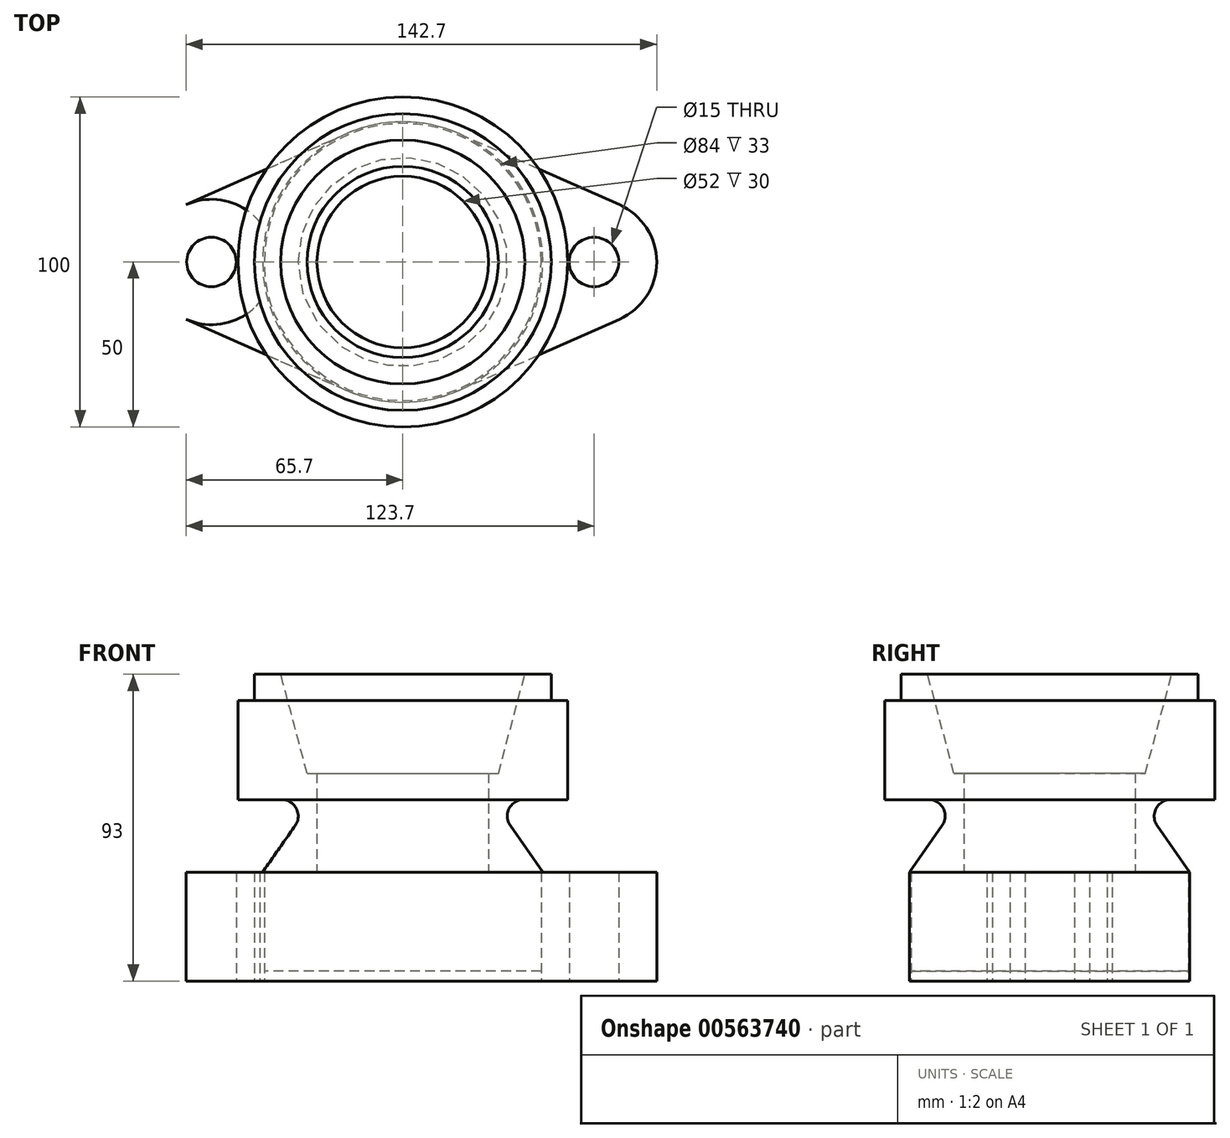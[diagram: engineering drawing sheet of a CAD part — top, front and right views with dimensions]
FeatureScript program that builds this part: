
annotation { "Feature Type Name" : "Feature", "Feature Type Description" : "" }
export const myFeature = defineFeature(function(context is Context, id is Id, definition is map)
    precondition{}
    {
        {
            var Q0;
            Q0=qCreatedBy(makeId("Top.planeOp"),FACE);
            var sketch = newSketch(context, id + "F0", { "sketchPlane" : qUnion([Q0])});
            skCircle(sketch, "E0", {"center": v(0, 0) * mm, "radius": 45 * mm});
            skCircle(sketch, "E1", {"center": v(0, 0) * mm, "radius": 42.5 * mm});
            skPoint(sketch, "E2", {"position": v(58, 0) * mm});
            skCircle(sketch, "E3", {"center": v(58, 0) * mm, "radius": 19 * mm});
            skCircle(sketch, "E4", {"center": v(58, 0) * mm, "radius": 7.5 * mm});
            skCircle(sketch, "E5.MirrorC", {"center": v(-58, 0) * mm, "radius": 7.5 * mm});
            skCircle(sketch, "E6.MirrorC", {"center": v(-58, 0) * mm, "radius": 19 * mm});
            skPoint(sketch, "E7", {"position": v(-20.17, 40.23) * mm});
            skPoint(sketch, "E8", {"position": v(20.17, 40.23) * mm});
            skPoint(sketch, "E9", {"position": v(20.17, -40.23) * mm});
            skPoint(sketch, "E10", {"position": v(-20.17, -40.23) * mm});
            skPoint(sketch, "E11", {"position": v(-77, 0) * mm});
            skPoint(sketch, "E12", {"position": v(73.15, 0) * mm});
            skLineSegment(sketch, "E13", {"start": v(-75.5, 13.02) * mm, "end": v(-3.42, 44.97) * mm});
            skLineSegment(sketch, "E14", {"start": v(12.58, 40.91) * mm, "end": v(100.28, 2.04) * mm});
            skLineSegment(sketch, "E15", {"start": v(-82.48, -9.93) * mm, "end": v(-3.7, -44.85) * mm});
            skLineSegment(sketch, "E16", {"start": v(12.55, -40.92) * mm, "end": v(81.15, -10.52) * mm});
            skCircle(sketch, "E17", {"center": v(0, 0) * mm, "radius": 42 * mm});
            skSolve(sketch);
        }
        {
            var Q0;
            Q0=qCreatedBy(makeId("Front.planeOp"),FACE);
            var sketch = newSketch(context, id + "F1", { "sketchPlane" : qUnion([Q0])});
            skLineSegment(sketch, "E18", {"start": v(-77, 0) * mm, "end": v(0, 0) * mm});
            skLineSegment(sketch, "E19", {"start": v(-77, 0) * mm, "end": v(-77, 33) * mm});
            skLineSegment(sketch, "E20", {"start": v(-77, 33) * mm, "end": v(-42.5, 33) * mm});
            skPoint(sketch, "E21", {"position": v(-42, 0) * mm});
            skLineSegment(sketch, "E22", {"start": v(-42, 0) * mm, "end": v(-42, 3) * mm});
            skLineSegment(sketch, "E23", {"start": v(-42, 3) * mm, "end": v(0, 3) * mm});
            skLineSegment(sketch, "E24", {"start": v(0, 2.9) * mm, "end": v(0, 3) * mm});
            skLineSegment(sketch, "E25", {"start": v(-42.5, 33) * mm, "end": v(-32.6, 47.13) * mm});
            skLineSegment(sketch, "E26", {"start": v(-36.7, 55) * mm, "end": v(-50, 55) * mm});
            skLineSegment(sketch, "E27", {"start": v(-50, 55) * mm, "end": v(-50, 85) * mm});
            skLineSegment(sketch, "E28", {"start": v(-50, 85) * mm, "end": v(-45, 85) * mm});
            skLineSegment(sketch, "E29", {"start": v(-45, 85) * mm, "end": v(-45, 93) * mm});
            skLineSegment(sketch, "E30", {"start": v(-45, 93) * mm, "end": v(-37, 93) * mm});
            skLineSegment(sketch, "E31", {"start": v(-29, 63) * mm, "end": v(-26, 63) * mm});
            skPoint(sketch, "E32", {"position": v(-29, 63) * mm});
            skLineSegment(sketch, "E33", {"start": v(-37, 93) * mm, "end": v(-29, 63) * mm});
            skPoint(sketch, "E34", {"position": v(-26, 63) * mm});
            skLineSegment(sketch, "E35", {"start": v(-26, 63) * mm, "end": v(-26, 21) * mm});
            skLineSegment(sketch, "E36", {"start": v(-26, 21) * mm, "end": v(0, 21) * mm});
            skLineSegment(sketch, "E37", {"start": v(0, 21) * mm, "end": v(0, 3) * mm});
            skLineSegment(sketch, "E38", {"start": v(-36.7, 59.99) * mm, "end": v(-36.7, 50) * mm, "construction": true});
            skLineSegment(sketch, "E39", {"start": v(-36.7, 50) * mm, "end": v(-27.85, 43.8) * mm, "construction": true});
            skPoint(sketch, "E40", {"position": v(-36.7, 55) * mm});
            skPoint(sketch, "E41", {"position": v(-32.6, 47.13) * mm});
            skArc(sketch, "E42", {"start": v(-32.6, 47.13) * mm, "mid": v(-32.27, 52.3) * mm, "end": v(-36.7, 55) * mm});
            skLineSegment(sketch, "E43", {"start": v(0, 21) * mm, "end": v(0, 51.34) * mm, "construction": true});
            skLineSegment(sketch, "E44", {"start": v(-42.5, 33) * mm, "end": v(-26, 33) * mm});
            skSolve(sketch);
        }
        {
            var Q0;
            Q0=makeQuery(id+"F1.imprint","IMPRINT",FACE,{"disambiguationData":[TD([[makeQuery(id+"F1.imprint","IMPRINT",EDGE,{"derivedFrom":sQuery(id+"F1.wireOp",EDGE,"E25")}),-1.0]])]});
            var Q1;
            Q1=sQuery(id+"F1.wireOp",EDGE,"E43");
            revolve(context, id + "F2", {"entities" : qUnion([Q0]), "axis" : qUnion([Q1]), "revolveType" : RevolveType.FULL});
        }
        {
            var Q0;
            {var subQ0=sQuery(id+"F0.wireOp",EDGE,"E14");var subQ1=sQuery(id+"F0.wireOp",EDGE,"E0");var subQ2=makeQuery(id+"F0.imprint","INTERSECT",VERTEX,{"derivedFrom":[subQ1,subQ0]});Q0=makeQuery(id+"F0.imprint","IMPRINT",FACE,{"disambiguationData":[TD([[makeQuery(id+"F0.imprint","IMPRINT",EDGE,{"disambiguationData":[TD([[subQ2,1.0]])],"derivedFrom":subQ1}),-1.0]])]});}
            var Q1;
            {var subQ0=sQuery(id+"F0.wireOp",EDGE,"E13");var subQ1=sQuery(id+"F0.wireOp",EDGE,"E0");var subQ2=makeQuery(id+"F0.imprint","INTERSECT",VERTEX,{"disambiguationData":[OD(1.0)],"derivedFrom":[subQ1,subQ0]});Q1=makeQuery(id+"F0.imprint","IMPRINT",FACE,{"disambiguationData":[TD([[makeQuery(id+"F0.imprint","IMPRINT",EDGE,{"disambiguationData":[TD([[subQ2,-1.0]])],"derivedFrom":subQ1}),-1.0]])]});}
            var Q2;
            {var subQ0=sQuery(id+"F0.wireOp",EDGE,"E15");var subQ1=sQuery(id+"F0.wireOp",EDGE,"E0");var subQ2=makeQuery(id+"F0.imprint","INTERSECT",VERTEX,{"disambiguationData":[OD(1.0)],"derivedFrom":[subQ1,subQ0]});Q2=makeQuery(id+"F0.imprint","IMPRINT",FACE,{"disambiguationData":[TD([[makeQuery(id+"F0.imprint","IMPRINT",EDGE,{"disambiguationData":[TD([[subQ2,1.0]])],"derivedFrom":subQ1}),-1.0]])]});}
            var Q3;
            {var subQ0=sQuery(id+"F0.wireOp",EDGE,"E16");var subQ1=sQuery(id+"F0.wireOp",EDGE,"E0");var subQ2=makeQuery(id+"F0.imprint","INTERSECT",VERTEX,{"derivedFrom":[subQ1,subQ0]});Q3=makeQuery(id+"F0.imprint","IMPRINT",FACE,{"disambiguationData":[TD([[makeQuery(id+"F0.imprint","IMPRINT",EDGE,{"disambiguationData":[TD([[subQ2,-1.0]])],"derivedFrom":subQ1}),-1.0]])]});}
            var Q4;
            {var subQ0=sQuery(id+"F0.wireOp",EDGE,"E14");var subQ1=sQuery(id+"F0.wireOp",EDGE,"E0");var subQ2=makeQuery(id+"F0.imprint","INTERSECT",VERTEX,{"derivedFrom":[subQ1,subQ0]});Q4=makeQuery(id+"F0.imprint","IMPRINT",FACE,{"disambiguationData":[TD([[makeQuery(id+"F0.imprint","IMPRINT",EDGE,{"disambiguationData":[TD([[subQ2,1.0]])],"derivedFrom":subQ1}),1.0]])]});}
            var Q5;
            {var subQ0=sQuery(id+"F0.wireOp",EDGE,"E13");var subQ1=sQuery(id+"F0.wireOp",EDGE,"E0");var subQ2=makeQuery(id+"F0.imprint","INTERSECT",VERTEX,{"disambiguationData":[OD(1.0)],"derivedFrom":[subQ1,subQ0]});Q5=makeQuery(id+"F0.imprint","IMPRINT",FACE,{"disambiguationData":[TD([[makeQuery(id+"F0.imprint","IMPRINT",EDGE,{"disambiguationData":[TD([[subQ2,-1.0]])],"derivedFrom":subQ1}),1.0]])]});}
            var Q6;
            Q6=makeQuery(id+"F0.imprint","IMPRINT",FACE,{"disambiguationData":[TD([[makeQuery(id+"F0.imprint","IMPRINT",EDGE,{"derivedFrom":sQuery(id+"F0.wireOp",EDGE,"E5.MirrorC")}),1.0]])]});
            var Q7;
            {var subQ0=sQuery(id+"F0.wireOp",EDGE,"E15");var subQ1=sQuery(id+"F0.wireOp",EDGE,"E0");var subQ2=makeQuery(id+"F0.imprint","INTERSECT",VERTEX,{"disambiguationData":[OD(1.0)],"derivedFrom":[subQ1,subQ0]});Q7=makeQuery(id+"F0.imprint","IMPRINT",FACE,{"disambiguationData":[TD([[makeQuery(id+"F0.imprint","IMPRINT",EDGE,{"disambiguationData":[TD([[subQ2,1.0]])],"derivedFrom":subQ1}),1.0]])]});}
            var Q8;
            {var subQ0=sQuery(id+"F0.wireOp",EDGE,"E16");var subQ1=sQuery(id+"F0.wireOp",EDGE,"E0");var subQ2=makeQuery(id+"F0.imprint","INTERSECT",VERTEX,{"derivedFrom":[subQ1,subQ0]});Q8=makeQuery(id+"F0.imprint","IMPRINT",FACE,{"disambiguationData":[TD([[makeQuery(id+"F0.imprint","IMPRINT",EDGE,{"disambiguationData":[TD([[subQ2,-1.0]])],"derivedFrom":subQ1}),1.0]])]});}
            var Q9;
            Q9=makeQuery(id+"F0.imprint","IMPRINT",FACE,{"disambiguationData":[TD([[makeQuery(id+"F0.imprint","IMPRINT",EDGE,{"derivedFrom":sQuery(id+"F0.wireOp",EDGE,"E4")}),-1.0]])]});
            var Q10;
            {var subQ0=sQuery(id+"F0.wireOp",EDGE,"E3");var subQ1=sQuery(id+"F0.wireOp",EDGE,"E0");var subQ2=makeQuery(id+"F0.imprint","INTERSECT",VERTEX,{"disambiguationData":[OD(0.0)],"derivedFrom":[subQ1,subQ0]});Q10=makeQuery(id+"F0.imprint","IMPRINT",FACE,{"disambiguationData":[TD([[makeQuery(id+"F0.imprint","IMPRINT",EDGE,{"disambiguationData":[TD([[subQ2,1.0]])],"derivedFrom":subQ1}),1.0]])]});}
            var Q11;
            {var subQ0=sQuery(id+"F0.wireOp",EDGE,"E6.MirrorC");var subQ1=sQuery(id+"F0.wireOp",EDGE,"E0");var subQ2=makeQuery(id+"F0.imprint","INTERSECT",VERTEX,{"disambiguationData":[OD(0.0)],"derivedFrom":[subQ1,subQ0]});Q11=makeQuery(id+"F0.imprint","IMPRINT",FACE,{"disambiguationData":[TD([[makeQuery(id+"F0.imprint","IMPRINT",EDGE,{"disambiguationData":[TD([[subQ2,-1.0]])],"derivedFrom":subQ1}),1.0]])]});}
            var Q12;
            {var subQ1=sQuery(id+"F0.wireOp",EDGE,"E1");var subQ7=sQuery(id+"F0.wireOp",EDGE,"E6.MirrorC");var subQ9=makeQuery(id+"F0.imprint","INTERSECT",VERTEX,{"disambiguationData":[OD(1.0)],"derivedFrom":[subQ1,subQ7]});Q12=makeQuery(id+"F0.imprint","IMPRINT",FACE,{"disambiguationData":[TD([[makeQuery(id+"F0.imprint","IMPRINT",EDGE,{"disambiguationData":[TD([[subQ9,-1.0]])],"derivedFrom":subQ1}),1.0]])]});}
            var Q13;
            {var subQ0=sQuery(id+"F0.wireOp",EDGE,"E1");var subQ4=makeQuery(id+"F0.imprint","INTERSECT",VERTEX,{"derivedFrom":[subQ0,sQuery(id+"F0.wireOp",EDGE,"E14")]});Q13=makeQuery(id+"F0.imprint","IMPRINT",FACE,{"disambiguationData":[TD([[makeQuery(id+"F0.imprint","IMPRINT",EDGE,{"disambiguationData":[TD([[subQ4,1.0]])],"derivedFrom":subQ0}),1.0]])]});}
            var Q14;
            {var subQ0=sQuery(id+"F0.wireOp",EDGE,"E3");var subQ1=sQuery(id+"F0.wireOp",EDGE,"E1");var subQ2=makeQuery(id+"F0.imprint","INTERSECT",VERTEX,{"disambiguationData":[OD(0.0)],"derivedFrom":[subQ1,subQ0]});Q14=makeQuery(id+"F0.imprint","IMPRINT",FACE,{"disambiguationData":[TD([[makeQuery(id+"F0.imprint","IMPRINT",EDGE,{"disambiguationData":[TD([[subQ2,1.0]])],"derivedFrom":subQ1}),1.0]])]});}
            var Q15;
            {var subQ0=sQuery(id+"F0.wireOp",EDGE,"E6.MirrorC");var subQ1=sQuery(id+"F0.wireOp",EDGE,"E1");var subQ2=makeQuery(id+"F0.imprint","INTERSECT",VERTEX,{"disambiguationData":[OD(0.0)],"derivedFrom":[subQ1,subQ0]});Q15=makeQuery(id+"F0.imprint","IMPRINT",FACE,{"disambiguationData":[TD([[makeQuery(id+"F0.imprint","IMPRINT",EDGE,{"disambiguationData":[TD([[subQ2,-1.0]])],"derivedFrom":subQ1}),1.0]])]});}
            extrude(context, id + "F3", {"entities" : qUnion([Q0, Q1, Q2, Q3, Q4, Q5, Q6, Q7, Q8, Q9, Q10, Q11, Q12, Q13, Q14, Q15]), "depth" : 33 * mm, "offsetDistance" : 25 * mm});
        }
        {
            var Q0;
            Q0=qCreatedBy(makeId("Top.planeOp"),FACE);
            var sketch = newSketch(context, id + "F4", { "sketchPlane" : qUnion([Q0])});
            skCircle(sketch, "E45", {"center": v(0, 0) * mm, "radius": 42 * mm});
            skSolve(sketch);
        }
        {
            var Q0;
            Q0=makeQuery(id+"F4.imprint","IMPRINT",FACE,{"disambiguationData":[TD([[makeQuery(id+"F4.imprint","IMPRINT",EDGE,{"derivedFrom":sQuery(id+"F4.wireOp",EDGE,"E45")}),1.0]])]});
            extrude(context, id + "F5", {"entities" : qUnion([Q0]), "depth" : 33 * mm, "offsetDistance" : 25 * mm, "hasSecondDirection" : true, "secondDirectionOppositeDirection" : true, "secondDirectionDepth" : -3 * mm});
        }
    });
